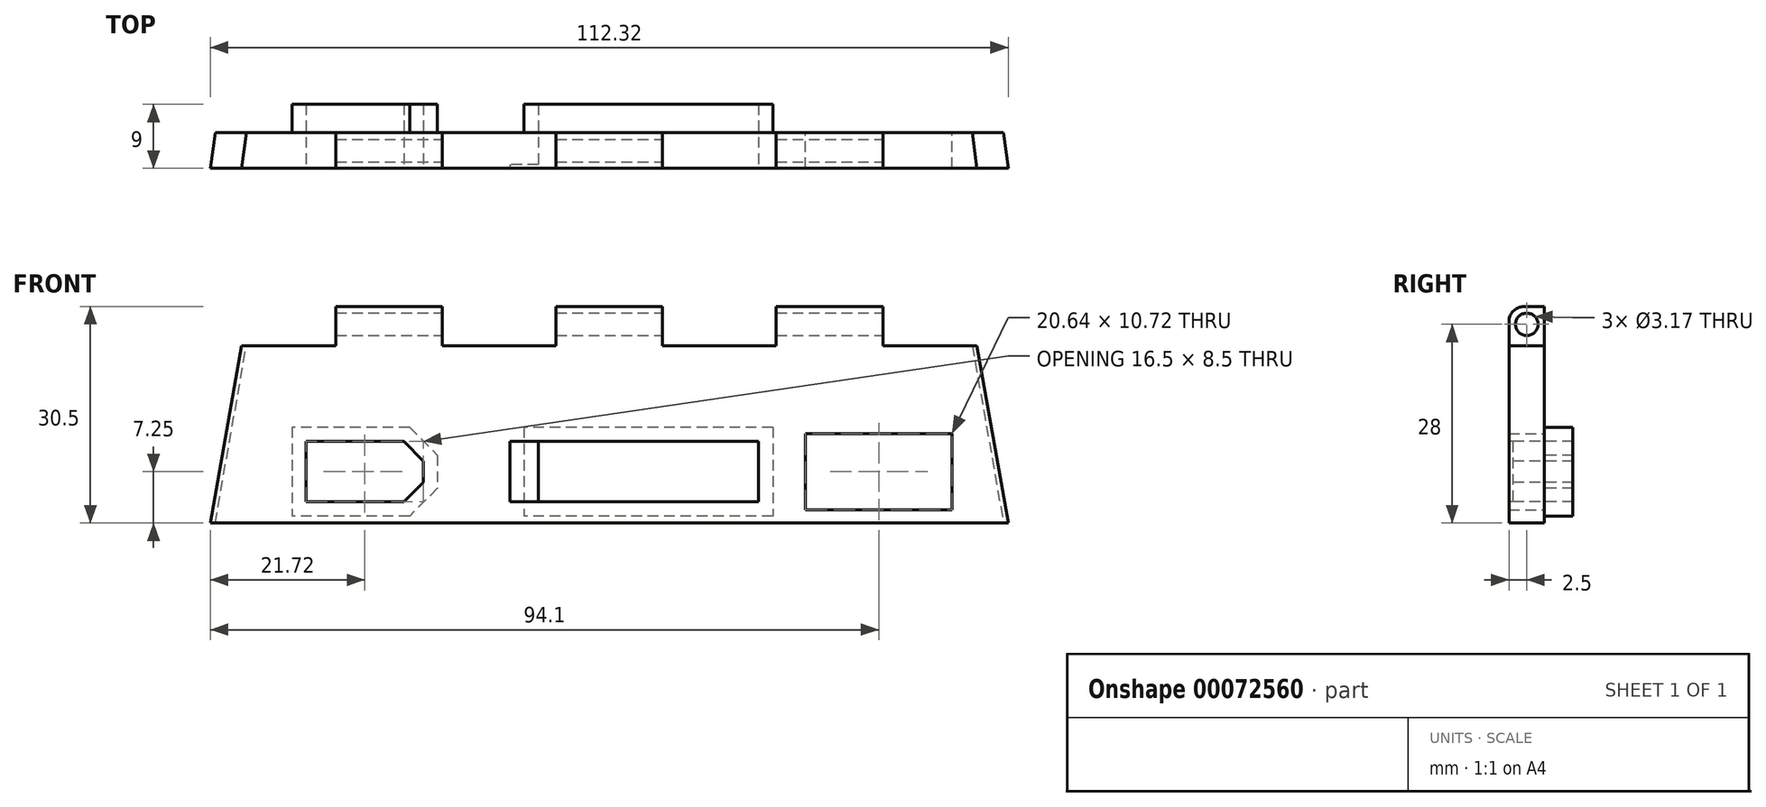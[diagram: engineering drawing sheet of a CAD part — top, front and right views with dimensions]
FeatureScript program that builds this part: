
annotation { "Feature Type Name" : "Feature", "Feature Type Description" : "" }
export const myFeature = defineFeature(function(context is Context, id is Id, definition is map)
    precondition{}
    {
        {
            var Q0;
            Q0=qCreatedBy(makeId("Front.planeOp"),FACE);
            var sketch = newSketch(context, id + "F0", { "sketchPlane" : qUnion([Q0])});
            skLineSegment(sketch, "E0.rect.bottom", {"start": v(15.5, 4.25) * mm, "end": v(-15.5, 4.25) * mm});
            skLineSegment(sketch, "E0.rect.top", {"start": v(15.5, -4.25) * mm, "end": v(-15.5, -4.25) * mm});
            skLineSegment(sketch, "E0.rect.left", {"start": v(15.5, 4.25) * mm, "end": v(15.5, -4.25) * mm});
            skLineSegment(sketch, "E0.rect.right", {"start": v(-15.5, 4.25) * mm, "end": v(-15.5, -4.25) * mm});
            skPoint(sketch, "E0.rect.middle", {"position": v(0, 0) * mm});
            skLineSegment(sketch, "E1.rect.bottom", {"start": v(37.19, 3.25) * mm, "end": v(27.69, 3.25) * mm});
            skLineSegment(sketch, "E1.rect.top", {"start": v(37.19, -3.25) * mm, "end": v(27.69, -3.25) * mm});
            skLineSegment(sketch, "E1.rect.left", {"start": v(37.19, 3.25) * mm, "end": v(37.19, -3.25) * mm});
            skLineSegment(sketch, "E1.rect.right", {"start": v(27.69, 3.25) * mm, "end": v(27.69, -3.25) * mm});
            skPoint(sketch, "E1.rect.middle", {"position": v(32.44, 0) * mm});
            skLineSegment(sketch, "E2.rect.bottom", {"start": v(-34.44, 4.25) * mm, "end": v(-48.19, 4.25) * mm});
            skLineSegment(sketch, "E2.rect.top", {"start": v(-34.44, -4.25) * mm, "end": v(-48.19, -4.25) * mm});
            skLineSegment(sketch, "E2.rect.right", {"start": v(-48.19, 4.25) * mm, "end": v(-48.19, -4.25) * mm});
            skPoint(sketch, "E2.rect.middle", {"position": v(-41.31, 0) * mm});
            skLineSegment(sketch, "E3", {"start": v(-34.44, 4.25) * mm, "end": v(-31.69, 1.5) * mm});
            skLineSegment(sketch, "E4", {"start": v(-31.69, 1.5) * mm, "end": v(-31.69, -1.5) * mm});
            skLineSegment(sketch, "E5", {"start": v(-31.69, -1.5) * mm, "end": v(-34.44, -4.25) * mm});
            skLineSegment(sketch, "E6.rect.bottom", {"start": v(-15.5, 4.25) * mm, "end": v(-19.5, 4.25) * mm, "construction": true});
            skLineSegment(sketch, "E6.rect.top", {"start": v(-15.5, -4.25) * mm, "end": v(-19.5, -4.25) * mm, "construction": true});
            skLineSegment(sketch, "E6.rect.left", {"start": v(-15.5, 4.25) * mm, "end": v(-15.5, -4.25) * mm, "construction": true});
            skLineSegment(sketch, "E6.rect.right", {"start": v(-19.5, 4.25) * mm, "end": v(-19.5, -4.25) * mm, "construction": true});
            skPoint(sketch, "E6.rect.middle", {"position": v(-17.5, 0) * mm});
            skPoint(sketch, "E7.endSnap0", {"position": v(37.19, 0) * mm});
            skPoint(sketch, "E8.endSnap0", {"position": v(-48.19, 0) * mm});
            skCircle(sketch, "E9", {"center": v(32.44, 8) * mm, "radius": 0.75 * mm, "construction": true});
            skLineSegment(sketch, "E10", {"start": v(-57.25, 17.75) * mm, "end": v(46.25, 17.75) * mm});
            skLineSegment(sketch, "E11", {"start": v(46.25, 17.75) * mm, "end": v(50.66, -7.25) * mm});
            skLineSegment(sketch, "E12", {"start": v(50.66, -7.25) * mm, "end": v(-61.66, -7.25) * mm});
            skLineSegment(sketch, "E13", {"start": v(-61.66, -7.25) * mm, "end": v(-57.25, 17.75) * mm});
            skLineSegment(sketch, "E14", {"start": v(-60.38, 0) * mm, "end": v(-48.19, 0) * mm, "construction": true});
            skLineSegment(sketch, "E15", {"start": v(-31.69, 0) * mm, "end": v(-19.5, 0) * mm, "construction": true});
            skLineSegment(sketch, "E16", {"start": v(15.5, 0) * mm, "end": v(27.69, 0) * mm, "construction": true});
            skLineSegment(sketch, "E17", {"start": v(37.19, 0) * mm, "end": v(49.38, 0) * mm, "construction": true});
            skSolve(sketch);
        }
        {
            var Q0;
            Q0 = qSketchRegion(id + "F0", true);
            extrude(context, id + "F1", {"entities" : qUnion([Q0]), "oppositeDirection" : true, "depth" : 5 * mm});
        }
        {
            var Q0;
            Q0=makeQuery(id+"F1.opExtrude","CAP_FACE",FACE,{"disambiguationData":[OSD([sQuery(id+"F0.wireOp",EDGE,"E0.rect.bottom"),sQuery(id+"F0.wireOp",EDGE,"E0.rect.top"),sQuery(id+"F0.wireOp",EDGE,"E0.rect.left"),sQuery(id+"F0.wireOp",EDGE,"E0.rect.right"),sQuery(id+"F0.wireOp",EDGE,"E1.rect.bottom"),sQuery(id+"F0.wireOp",EDGE,"E1.rect.top"),sQuery(id+"F0.wireOp",EDGE,"E1.rect.left"),sQuery(id+"F0.wireOp",EDGE,"E1.rect.right"),sQuery(id+"F0.wireOp",EDGE,"E2.rect.bottom"),sQuery(id+"F0.wireOp",EDGE,"E2.rect.top"),sQuery(id+"F0.wireOp",EDGE,"E2.rect.right"),sQuery(id+"F0.wireOp",EDGE,"E3"),sQuery(id+"F0.wireOp",EDGE,"E4"),sQuery(id+"F0.wireOp",EDGE,"E5"),sQuery(id+"F0.wireOp",EDGE,"E9"),sQuery(id+"F0.wireOp",EDGE,"E10"),sQuery(id+"F0.wireOp",EDGE,"E11"),sQuery(id+"F0.wireOp",EDGE,"E12"),sQuery(id+"F0.wireOp",EDGE,"E13")])],"isStart":true});
            var sketch = newSketch(context, id + "F2", { "sketchPlane" : qUnion([Q0])});
            skLineSegment(sketch, "E18.bottom", {"start": v(-15.5, 4.25) * mm, "end": v(-19.5, 4.25) * mm});
            skLineSegment(sketch, "E18.top", {"start": v(-15.5, -4.25) * mm, "end": v(-19.5, -4.25) * mm});
            skLineSegment(sketch, "E18.left", {"start": v(-15.5, 4.25) * mm, "end": v(-15.5, -4.25) * mm});
            skLineSegment(sketch, "E18.right", {"start": v(-19.5, 4.25) * mm, "end": v(-19.5, -4.25) * mm});
            skPoint(sketch, "E19.0", {"position": v(-19.5, -4.25) * mm});
            skSolve(sketch);
        }
        {
            var Q0;
            Q0 = qSketchRegion(id + "F2", true);
            extrude(context, id + "F3", {"entities" : qUnion([Q0]), "operationType" : NewBodyOperationType.REMOVE, "oppositeDirection" : true, "depth" : 0.5 * mm});
        }
        {
            var Q0;
            Q0=makeQuery(id+"F1.opExtrude","CAP_FACE",FACE,{"disambiguationData":[OSD([sQuery(id+"F0.wireOp",EDGE,"E0.rect.bottom"),sQuery(id+"F0.wireOp",EDGE,"E0.rect.top"),sQuery(id+"F0.wireOp",EDGE,"E0.rect.left"),sQuery(id+"F0.wireOp",EDGE,"E0.rect.right"),sQuery(id+"F0.wireOp",EDGE,"E1.rect.bottom"),sQuery(id+"F0.wireOp",EDGE,"E1.rect.top"),sQuery(id+"F0.wireOp",EDGE,"E1.rect.left"),sQuery(id+"F0.wireOp",EDGE,"E1.rect.right"),sQuery(id+"F0.wireOp",EDGE,"E2.rect.bottom"),sQuery(id+"F0.wireOp",EDGE,"E2.rect.top"),sQuery(id+"F0.wireOp",EDGE,"E2.rect.right"),sQuery(id+"F0.wireOp",EDGE,"E3"),sQuery(id+"F0.wireOp",EDGE,"E4"),sQuery(id+"F0.wireOp",EDGE,"E5"),sQuery(id+"F0.wireOp",EDGE,"E9"),sQuery(id+"F0.wireOp",EDGE,"E10"),sQuery(id+"F0.wireOp",EDGE,"E11"),sQuery(id+"F0.wireOp",EDGE,"E12"),sQuery(id+"F0.wireOp",EDGE,"E13")])],"isStart":false});
            var sketch = newSketch(context, id + "F4", { "sketchPlane" : qUnion([Q0])});
            skLineSegment(sketch, "E20.rect.bottom", {"start": v(-22.12, 5.36) * mm, "end": v(-42.76, 5.36) * mm});
            skLineSegment(sketch, "E20.rect.top", {"start": v(-22.12, -5.36) * mm, "end": v(-42.76, -5.36) * mm});
            skLineSegment(sketch, "E20.rect.left", {"start": v(-22.12, 5.36) * mm, "end": v(-22.12, -5.36) * mm});
            skLineSegment(sketch, "E20.rect.right", {"start": v(-42.76, 5.36) * mm, "end": v(-42.76, -5.36) * mm});
            skPoint(sketch, "E20.rect.middle", {"position": v(-32.44, 0) * mm});
            skCircle(sketch, "E21.0", {"center": v(-32.44, 8.52) * mm, "radius": 0.75 * mm, "construction": true});
            skLineSegment(sketch, "E22.0", {"start": v(-37.19, 3.25) * mm, "end": v(-27.69, 3.25) * mm});
            skPoint(sketch, "E23", {"position": v(-32.44, 3.25) * mm});
            skSolve(sketch);
        }
        {
            var Q0;
            Q0 = qSketchRegion(id + "F4", true);
            extrude(context, id + "F5", {"entities" : qUnion([Q0]), "operationType" : NewBodyOperationType.REMOVE, "oppositeDirection" : true, "depth" : 5 * mm - 2 / 812.8 * mm});
        }
        {
            var Q0;
            Q0=makeQuery(id+"F1.opExtrude","CAP_FACE",FACE,{"disambiguationData":[OSD([sQuery(id+"F0.wireOp",EDGE,"E0.rect.bottom"),sQuery(id+"F0.wireOp",EDGE,"E0.rect.top"),sQuery(id+"F0.wireOp",EDGE,"E0.rect.left"),sQuery(id+"F0.wireOp",EDGE,"E0.rect.right"),sQuery(id+"F0.wireOp",EDGE,"E1.rect.bottom"),sQuery(id+"F0.wireOp",EDGE,"E1.rect.top"),sQuery(id+"F0.wireOp",EDGE,"E1.rect.left"),sQuery(id+"F0.wireOp",EDGE,"E1.rect.right"),sQuery(id+"F0.wireOp",EDGE,"E2.rect.bottom"),sQuery(id+"F0.wireOp",EDGE,"E2.rect.top"),sQuery(id+"F0.wireOp",EDGE,"E2.rect.right"),sQuery(id+"F0.wireOp",EDGE,"E3"),sQuery(id+"F0.wireOp",EDGE,"E4"),sQuery(id+"F0.wireOp",EDGE,"E5"),sQuery(id+"F0.wireOp",EDGE,"E9"),sQuery(id+"F0.wireOp",EDGE,"E10"),sQuery(id+"F0.wireOp",EDGE,"E11"),sQuery(id+"F0.wireOp",EDGE,"E12"),sQuery(id+"F0.wireOp",EDGE,"E13")])],"isStart":true});
            var sketch = newSketch(context, id + "F6", { "sketchPlane" : qUnion([Q0])});
            skLineSegment(sketch, "E24", {"start": v(-18.5, 2.9) * mm, "end": v(-16.5, 2.9) * mm});
            skLineSegment(sketch, "E25", {"start": v(-18.5, 0.4) * mm, "end": v(-17.5, 0.4) * mm});
            skPoint(sketch, "E26.endSnap0", {"position": v(-17.5, 0.4) * mm});
            skLineSegment(sketch, "E27", {"start": v(-17.5, 1.4) * mm, "end": v(-17.5, 0.4) * mm});
            skArc(sketch, "E28", {"start": v(-17.1, -2.3) * mm, "mid": v(-17.78, -2.02) * mm, "end": v(-17.5, -2.7) * mm});
            skArc(sketch, "E29", {"start": v(-17.9, -3.1) * mm, "mid": v(-17.22, -3.38) * mm, "end": v(-17.5, -2.7) * mm});
            skPoint(sketch, "E30", {"position": v(-17.1, -2.3) * mm});
            skPoint(sketch, "E31", {"position": v(-17.9, -3.1) * mm});
            skLineSegment(sketch, "E32", {"start": v(-17.5, 0.4) * mm, "end": v(-16.5, 0.4) * mm});
            skLineSegment(sketch, "E33", {"start": v(-17.5, 0.4) * mm, "end": v(-17.5, -0.6) * mm});
            skSolve(sketch);
        }
        {
            var Q0;
            Q0=makeQuery(id+"F1.opExtrude","CAP_EDGE",EDGE,{"disambiguationData":[OSD([sQuery(id+"F0.wireOp",EDGE,"E13")])],"isStart":false});
            var Q1;
            Q1=makeQuery(id+"F1.opExtrude","CAP_EDGE",EDGE,{"disambiguationData":[OSD([sQuery(id+"F0.wireOp",EDGE,"E11")])],"isStart":false});
            chamfer(context, id + "F7", {"entities" : qUnion([Q0, Q1]), "chamferType" : ChamferType.OFFSET_ANGLE, "width" : 5 * mm, "oppositeDirection" : true, "angle" : 7.5 * degree, "tangentPropagation" : true});
        }
        {
            var Q0;
            Q0=makeQuery(id+"F1.opExtrude","CAP_FACE",FACE,{"disambiguationData":[OSD([sQuery(id+"F0.wireOp",EDGE,"E0.rect.bottom"),sQuery(id+"F0.wireOp",EDGE,"E0.rect.top"),sQuery(id+"F0.wireOp",EDGE,"E0.rect.left"),sQuery(id+"F0.wireOp",EDGE,"E0.rect.right"),sQuery(id+"F0.wireOp",EDGE,"E1.rect.bottom"),sQuery(id+"F0.wireOp",EDGE,"E1.rect.top"),sQuery(id+"F0.wireOp",EDGE,"E1.rect.left"),sQuery(id+"F0.wireOp",EDGE,"E1.rect.right"),sQuery(id+"F0.wireOp",EDGE,"E2.rect.bottom"),sQuery(id+"F0.wireOp",EDGE,"E2.rect.top"),sQuery(id+"F0.wireOp",EDGE,"E2.rect.right"),sQuery(id+"F0.wireOp",EDGE,"E3"),sQuery(id+"F0.wireOp",EDGE,"E4"),sQuery(id+"F0.wireOp",EDGE,"E5"),sQuery(id+"F0.wireOp",EDGE,"E9"),sQuery(id+"F0.wireOp",EDGE,"E10"),sQuery(id+"F0.wireOp",EDGE,"E11"),sQuery(id+"F0.wireOp",EDGE,"E12"),sQuery(id+"F0.wireOp",EDGE,"E13")])],"isStart":false});
            var sketch = newSketch(context, id + "F8", { "sketchPlane" : qUnion([Q0])});
            skLineSegment(sketch, "E34.0", {"start": v(-15.5, 4.25) * mm, "end": v(15.5, 4.25) * mm});
            skLineSegment(sketch, "E34.1", {"start": v(15.5, 4.25) * mm, "end": v(15.5, -4.25) * mm});
            skLineSegment(sketch, "E34.2", {"start": v(-15.5, -4.25) * mm, "end": v(15.5, -4.25) * mm});
            skLineSegment(sketch, "E34.3", {"start": v(-15.5, 4.25) * mm, "end": v(-15.5, -4.25) * mm});
            skLineSegment(sketch, "E35.0", {"start": v(-17.5, 6.25) * mm, "end": v(17.5, 6.25) * mm});
            skLineSegment(sketch, "E35.1", {"start": v(-17.5, 6.25) * mm, "end": v(-17.5, -6.25) * mm});
            skLineSegment(sketch, "E35.2", {"start": v(-17.5, -6.25) * mm, "end": v(17.5, -6.25) * mm});
            skLineSegment(sketch, "E35.3", {"start": v(17.5, 6.25) * mm, "end": v(17.5, -6.25) * mm});
            skSolve(sketch);
        }
        {
            var Q0;
            Q0 = qSketchRegion(id + "F8", true);
            extrude(context, id + "F9", {"entities" : qUnion([Q0]), "operationType" : NewBodyOperationType.ADD, "depth" : 4 * mm});
        }
        {
            var Q0;
            Q0=makeQuery(id+"F1.opExtrude","CAP_FACE",FACE,{"disambiguationData":[OSD([sQuery(id+"F0.wireOp",EDGE,"E0.rect.bottom"),sQuery(id+"F0.wireOp",EDGE,"E0.rect.top"),sQuery(id+"F0.wireOp",EDGE,"E0.rect.left"),sQuery(id+"F0.wireOp",EDGE,"E0.rect.right"),sQuery(id+"F0.wireOp",EDGE,"E1.rect.bottom"),sQuery(id+"F0.wireOp",EDGE,"E1.rect.top"),sQuery(id+"F0.wireOp",EDGE,"E1.rect.left"),sQuery(id+"F0.wireOp",EDGE,"E1.rect.right"),sQuery(id+"F0.wireOp",EDGE,"E2.rect.bottom"),sQuery(id+"F0.wireOp",EDGE,"E2.rect.top"),sQuery(id+"F0.wireOp",EDGE,"E2.rect.right"),sQuery(id+"F0.wireOp",EDGE,"E3"),sQuery(id+"F0.wireOp",EDGE,"E4"),sQuery(id+"F0.wireOp",EDGE,"E5"),sQuery(id+"F0.wireOp",EDGE,"E9"),sQuery(id+"F0.wireOp",EDGE,"E10"),sQuery(id+"F0.wireOp",EDGE,"E11"),sQuery(id+"F0.wireOp",EDGE,"E12"),sQuery(id+"F0.wireOp",EDGE,"E13")])],"isStart":false});
            var sketch = newSketch(context, id + "F10", { "sketchPlane" : qUnion([Q0])});
            skLineSegment(sketch, "E36.0", {"start": v(34.44, 4.25) * mm, "end": v(48.19, 4.25) * mm});
            skLineSegment(sketch, "E36.1", {"start": v(48.19, 4.25) * mm, "end": v(48.19, -4.25) * mm});
            skLineSegment(sketch, "E36.2", {"start": v(34.44, -4.25) * mm, "end": v(48.19, -4.25) * mm});
            skLineSegment(sketch, "E36.3", {"start": v(31.69, -1.5) * mm, "end": v(34.44, -4.25) * mm});
            skLineSegment(sketch, "E36.4", {"start": v(31.69, 1.5) * mm, "end": v(31.69, -1.5) * mm});
            skLineSegment(sketch, "E36.5", {"start": v(34.44, 4.25) * mm, "end": v(31.69, 1.5) * mm});
            skLineSegment(sketch, "E37.0", {"start": v(33.61, 6.25) * mm, "end": v(50.19, 6.25) * mm});
            skLineSegment(sketch, "E37.1", {"start": v(29.69, 2.33) * mm, "end": v(29.69, -2.33) * mm});
            skLineSegment(sketch, "E37.2", {"start": v(29.69, -2.33) * mm, "end": v(33.61, -6.25) * mm});
            skLineSegment(sketch, "E37.3", {"start": v(33.61, 6.25) * mm, "end": v(29.69, 2.33) * mm});
            skLineSegment(sketch, "E37.4", {"start": v(33.61, -6.25) * mm, "end": v(50.19, -6.25) * mm});
            skLineSegment(sketch, "E37.5", {"start": v(50.19, 6.25) * mm, "end": v(50.19, -6.25) * mm});
            skSolve(sketch);
        }
        {
            var Q0;
            Q0 = qSketchRegion(id + "F10", true);
            extrude(context, id + "F11", {"entities" : qUnion([Q0]), "operationType" : NewBodyOperationType.ADD, "depth" : 4 * mm});
        }
        {
            var Q0;
            Q0=makeQuery(id+"F1.opExtrude","SWEPT_FACE",FACE,{"disambiguationData":[OSD([sQuery(id+"F0.wireOp",EDGE,"E10")])]});
            var sketch = newSketch(context, id + "F12", { "sketchPlane" : qUnion([Q0])});
            skLineSegment(sketch, "E38.bottom", {"start": v(-44, 5) * mm, "end": v(-29, 5) * mm});
            skLineSegment(sketch, "E38.top", {"start": v(-44, 0) * mm, "end": v(-29, 0) * mm});
            skLineSegment(sketch, "E38.left", {"start": v(-44, 5) * mm, "end": v(-44, 0) * mm});
            skLineSegment(sketch, "E38.right", {"start": v(-29, 5) * mm, "end": v(-29, 0) * mm});
            skLineSegment(sketch, "E39.bottom", {"start": v(18, 5) * mm, "end": v(33, 5) * mm});
            skLineSegment(sketch, "E39.top", {"start": v(18, 0) * mm, "end": v(33, 0) * mm});
            skLineSegment(sketch, "E39.left", {"start": v(18, 5) * mm, "end": v(18, 0) * mm});
            skLineSegment(sketch, "E39.right", {"start": v(33, 5) * mm, "end": v(33, 0) * mm});
            skLineSegment(sketch, "E40", {"start": v(-56.92, 2.5) * mm, "end": v(-44, 2.5) * mm, "construction": true});
            skLineSegment(sketch, "E41", {"start": v(33, 2.5) * mm, "end": v(45.92, 2.5) * mm, "construction": true});
            skLineSegment(sketch, "E42.bottom", {"start": v(-13, 5) * mm, "end": v(2, 5) * mm});
            skLineSegment(sketch, "E42.top", {"start": v(-13, 0) * mm, "end": v(2, 0) * mm});
            skLineSegment(sketch, "E42.left", {"start": v(-13, 5) * mm, "end": v(-13, 0) * mm});
            skLineSegment(sketch, "E42.right", {"start": v(2, 5) * mm, "end": v(2, 0) * mm});
            skLineSegment(sketch, "E43", {"start": v(-29, 2.5) * mm, "end": v(-13, 2.5) * mm, "construction": true});
            skLineSegment(sketch, "E44", {"start": v(2, 2.5) * mm, "end": v(18, 2.5) * mm, "construction": true});
            skSolve(sketch);
        }
        {
            var Q0;
            Q0 = qSketchRegion(id + "F12", true);
            extrude(context, id + "F13", {"entities" : qUnion([Q0]), "operationType" : NewBodyOperationType.ADD, "depth" : 5.5 * mm});
        }
        {
            var Q0;
            Q0=makeQuery(id+"F13.opExtrude","SWEPT_FACE",FACE,{"disambiguationData":[OSD([sQuery(id+"F12.wireOp",EDGE,"E39.right")])]});
            var sketch = newSketch(context, id + "F14", { "sketchPlane" : qUnion([Q0])});
            skCircle(sketch, "E45", {"center": v(2.5, 20.75) * mm, "radius": 1.59 * mm});
            skLineSegment(sketch, "E46", {"start": v(2.5, 22.34) * mm, "end": v(2.5, 23.25) * mm, "construction": true});
            skLineSegment(sketch, "E47", {"start": v(0, 20.75) * mm, "end": v(0.91, 20.75) * mm, "construction": true});
            skSolve(sketch);
        }
        {
            var Q0;
            Q0 = qSketchRegion(id + "F14", true);
            extrude(context, id + "F15", {"entities" : qUnion([Q0]), "operationType" : NewBodyOperationType.REMOVE, "endBound" : BoundingType.THROUGH_ALL, "oppositeDirection" : true, "depth" : 25 * mm});
        }
        {
            var Q0;
            Q0=makeQuery(id+"F13.opExtrude","CAP_EDGE",EDGE,{"disambiguationData":[OSD([sQuery(id+"F12.wireOp",EDGE,"E38.top")])],"isStart":false});
            var Q1;
            Q1=makeQuery(id+"F13.opExtrude","CAP_EDGE",EDGE,{"disambiguationData":[OSD([sQuery(id+"F12.wireOp",EDGE,"E42.top")])],"isStart":false});
            var Q2;
            Q2=makeQuery(id+"F13.opExtrude","CAP_EDGE",EDGE,{"disambiguationData":[OSD([sQuery(id+"F12.wireOp",EDGE,"E39.top")])],"isStart":false});
            fillet(context, id + "F16", {"entities" : qUnion([Q0, Q1, Q2]), "radius" : 2.1 * mm, "tangentPropagation" : true, "allowEdgeOverflow" : false});
        }
    });
